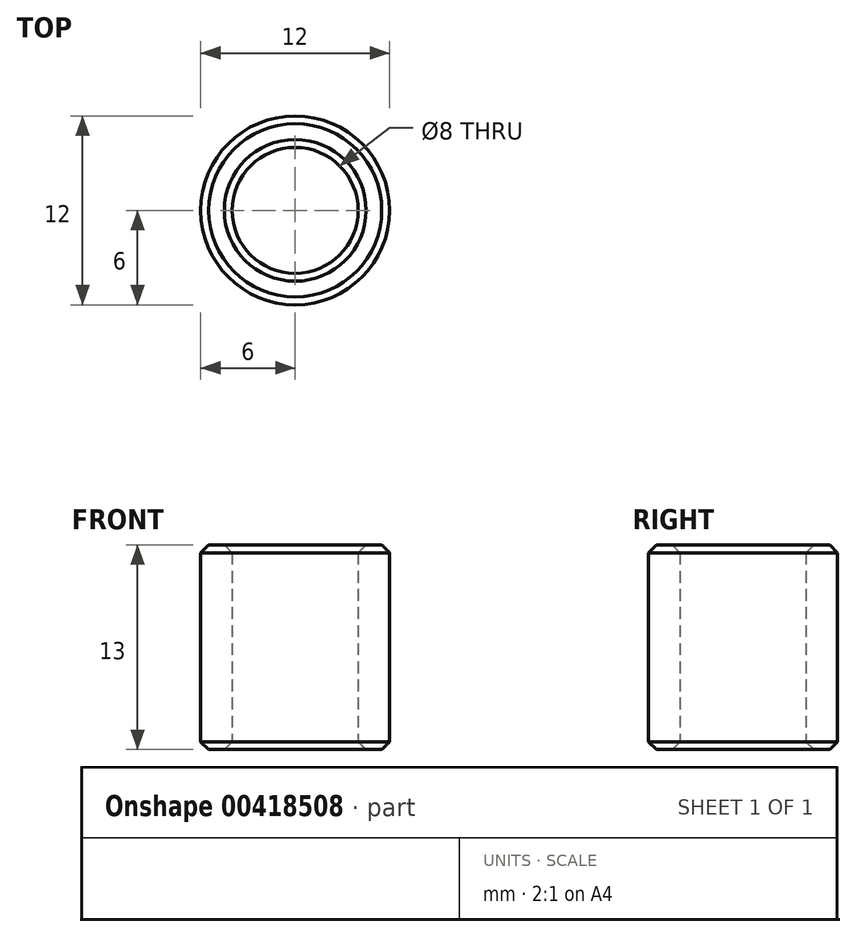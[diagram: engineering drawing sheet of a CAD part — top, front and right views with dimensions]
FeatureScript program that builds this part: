
annotation { "Feature Type Name" : "Feature", "Feature Type Description" : "" }
export const myFeature = defineFeature(function(context is Context, id is Id, definition is map)
    precondition{}
    {
        {
            var Q0;
            Q0=qCreatedBy(makeId("Top.planeOp"),FACE);
            var sketch = newSketch(context, id + "F0", { "sketchPlane" : qUnion([Q0])});
            skCircle(sketch, "E0", {"center": v(0, 0) * mm, "radius": 4 * mm});
            skCircle(sketch, "E1", {"center": v(0, 0) * mm, "radius": 6 * mm});
            skSolve(sketch);
        }
        {
            var Q0;
            Q0 = qSketchRegion(id + "F0", true);
            extrude(context, id + "F1", {"entities" : qUnion([Q0]), "depth" : 13 * mm});
        }
        {
            var Q0;
            Q0=makeQuery(id+"F1.opExtrude","CAP_EDGE",EDGE,{"disambiguationData":[OSD([sQuery(id+"F0.wireOp",EDGE,"E0")])],"isStart":false});
            chamfer(context, id + "F2", {"entities" : qUnion([Q0]), "width" : .5 * mm, "tangentPropagation" : true});
        }
        {
            var Q0;
            Q0=makeQuery(id+"F1.opExtrude","CAP_EDGE",EDGE,{"disambiguationData":[OSD([sQuery(id+"F0.wireOp",EDGE,"E0")])],"isStart":true});
            chamfer(context, id + "F3", {"entities" : qUnion([Q0]), "width" : .5 * mm, "tangentPropagation" : true});
        }
        {
            var Q0;
            Q0=makeQuery(id+"F1.opExtrude","CAP_EDGE",EDGE,{"disambiguationData":[OSD([sQuery(id+"F0.wireOp",EDGE,"E1")])],"isStart":true});
            var Q1;
            Q1=makeQuery(id+"F1.opExtrude","CAP_EDGE",EDGE,{"disambiguationData":[OSD([sQuery(id+"F0.wireOp",EDGE,"E1")])],"isStart":false});
            chamfer(context, id + "F4", {"entities" : qUnion([Q0, Q1]), "width" : .5 * mm, "tangentPropagation" : true});
        }
    });
